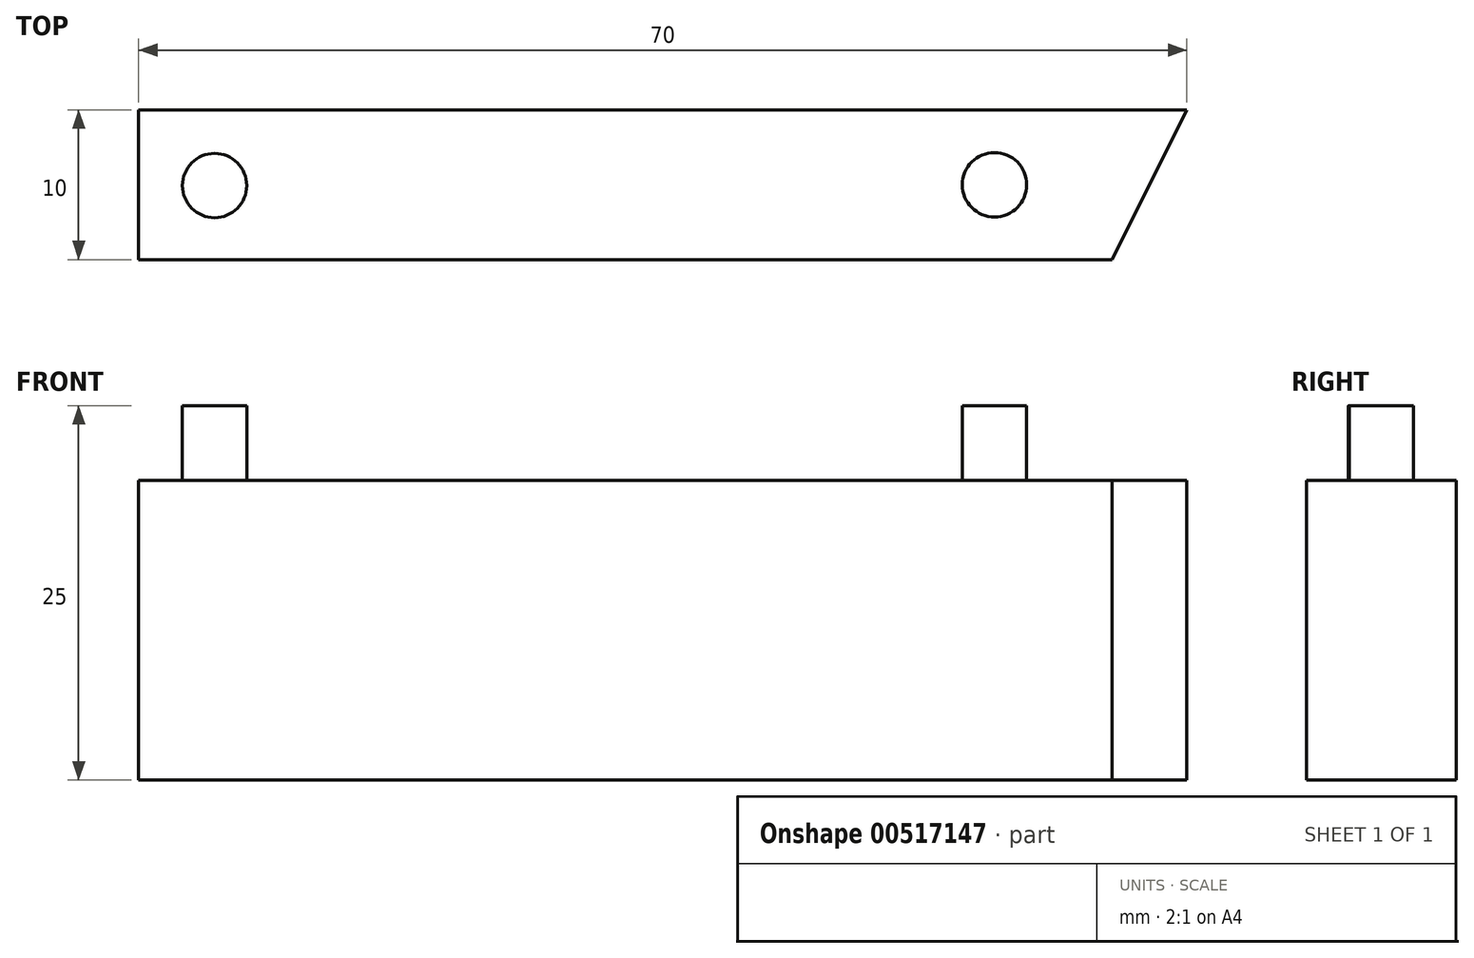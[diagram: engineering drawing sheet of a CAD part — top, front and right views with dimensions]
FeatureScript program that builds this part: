
annotation { "Feature Type Name" : "Feature", "Feature Type Description" : "" }
export const myFeature = defineFeature(function(context is Context, id is Id, definition is map)
    precondition{}
    {
        {
            var Q0;
            Q0=qCreatedBy(makeId("Top.planeOp"),FACE);
            var sketch = newSketch(context, id + "F0", { "sketchPlane" : qUnion([Q0])});
            skLineSegment(sketch, "E0", {"start": v(-27.28, 33.89) * mm, "end": v(42.72, 33.89) * mm});
            skLineSegment(sketch, "E1", {"start": v(-27.28, 33.89) * mm, "end": v(-27.28, 23.89) * mm});
            skLineSegment(sketch, "E2", {"start": v(-27.28, 23.89) * mm, "end": v(37.72, 23.89) * mm});
            skLineSegment(sketch, "E3", {"start": v(37.72, 23.89) * mm, "end": v(42.72, 33.89) * mm});
            skSolve(sketch);
        }
        {
            var Q0;
            Q0=makeQuery(id+"F0.imprint","IMPRINT",FACE,{"disambiguationData":[TD([[makeQuery(id+"F0.imprint","IMPRINT",EDGE,{"derivedFrom":sQuery(id+"F0.wireOp",EDGE,"E0")}),-1.0]])]});
            extrude(context, id + "F1", {"entities" : qUnion([Q0]), "depth" : 20 * mm, "offsetDistance" : 25 * mm});
        }
        {
            var Q0;
            Q0=makeQuery(id+"F1.opExtrude","CAP_FACE",FACE,{"disambiguationData":[OSD([sQuery(id+"F0.wireOp",EDGE,"E0"),sQuery(id+"F0.wireOp",EDGE,"E1"),sQuery(id+"F0.wireOp",EDGE,"E2"),sQuery(id+"F0.wireOp",EDGE,"E3")])],"isStart":false});
            var sketch = newSketch(context, id + "F2", { "sketchPlane" : qUnion([Q0])});
            skCircle(sketch, "E4", {"center": v(-22.2, 28.84) * mm, "radius": 2.15 * mm});
            skCircle(sketch, "E5", {"center": v(29.88, 28.89) * mm, "radius": 2.15 * mm});
            skPoint(sketch, "E5.centerSnap0", {"position": v(40.22, 28.89) * mm});
            skSolve(sketch);
        }
        {
            var Q0;
            Q0=makeQuery(id+"F2.imprint","IMPRINT",FACE,{"disambiguationData":[TD([[makeQuery(id+"F2.imprint","IMPRINT",EDGE,{"derivedFrom":sQuery(id+"F2.wireOp",EDGE,"E4")}),1.0]])]});
            var Q1;
            Q1=makeQuery(id+"F2.imprint","IMPRINT",FACE,{"disambiguationData":[TD([[makeQuery(id+"F2.imprint","IMPRINT",EDGE,{"derivedFrom":sQuery(id+"F2.wireOp",EDGE,"E5")}),1.0]])]});
            extrude(context, id + "F3", {"entities" : qUnion([Q0, Q1]), "operationType" : NewBodyOperationType.ADD, "depth" : 5 * mm, "offsetDistance" : 25 * mm});
        }
    });
